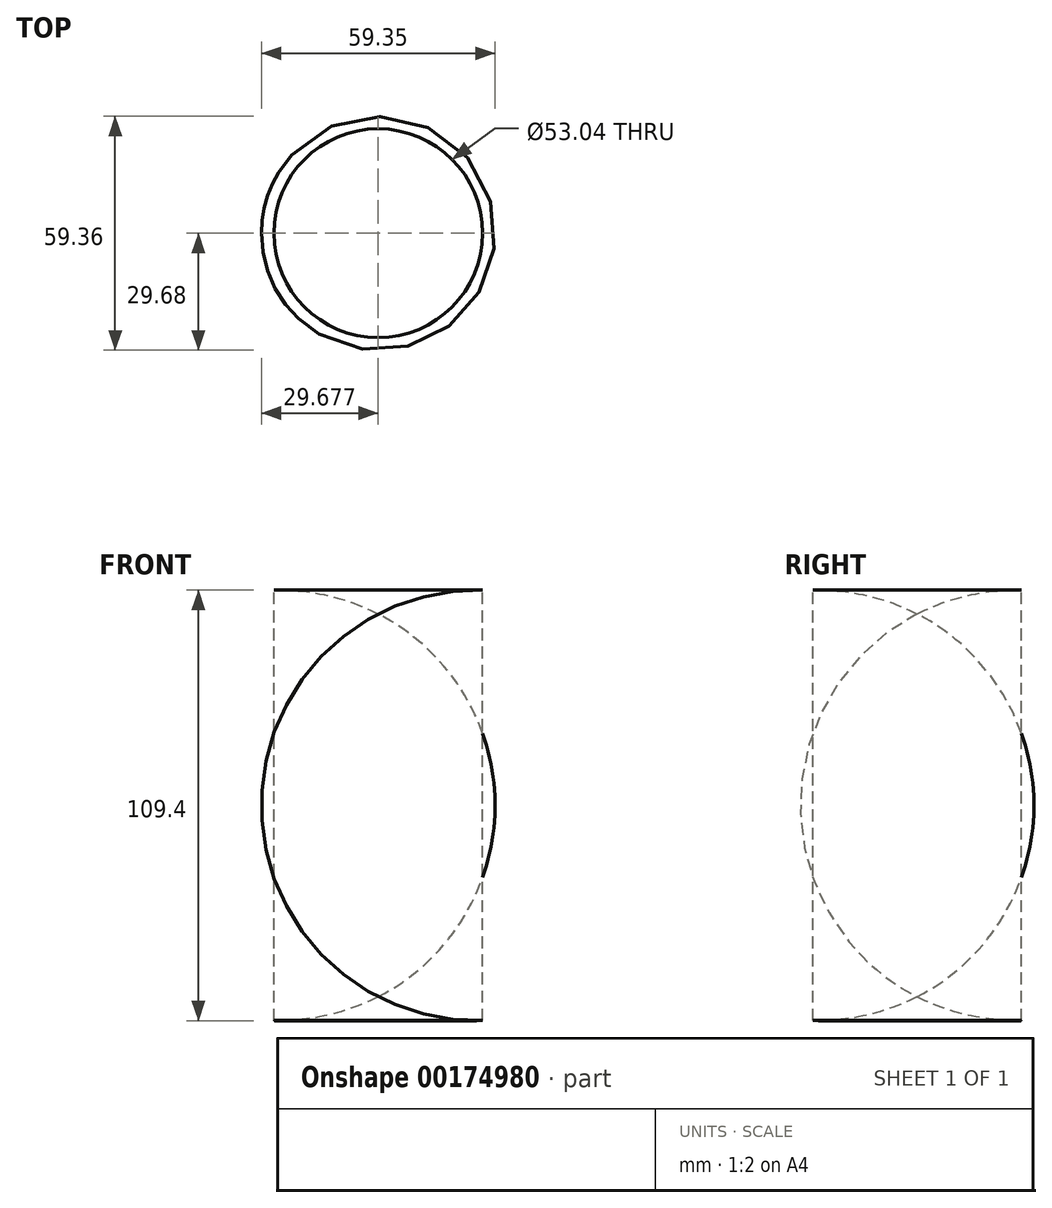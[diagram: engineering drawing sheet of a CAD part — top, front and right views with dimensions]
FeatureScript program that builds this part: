
annotation { "Feature Type Name" : "Feature", "Feature Type Description" : "" }
export const myFeature = defineFeature(function(context is Context, id is Id, definition is map)
    precondition{}
    {
        {
            var Q0;
            Q0=qCreatedBy(makeId("Front.planeOp"),FACE);
            var sketch = newSketch(context, id + "F0", { "sketchPlane" : qUnion([Q0])});
            skLineSegment(sketch, "E0", {"start": v(-43.95, 62.73) * mm, "end": v(-43.95, -46.64) * mm});
            skLineSegment(sketch, "E1", {"start": v(-17.43, 62.13) * mm, "end": v(-17.43, -47.23) * mm});
            skArc(sketch, "E2", {"start": v(-17.43, -47.23) * mm, "mid": v(35.77, 7.45) * mm, "end": v(-17.43, 62.13) * mm});
            skSolve(sketch);
        }
        {
            var Q0;
            Q0 = qSketchRegion(id + "F0", true);
            var Q1;
            Q1=sQuery(id+"F0.wireOp",EDGE,"E0");
            revolve(context, id + "F1", {"entities" : qUnion([Q0]), "axis" : qUnion([Q1]), "revolveType" : RevolveType.FULL});
        }
    });
